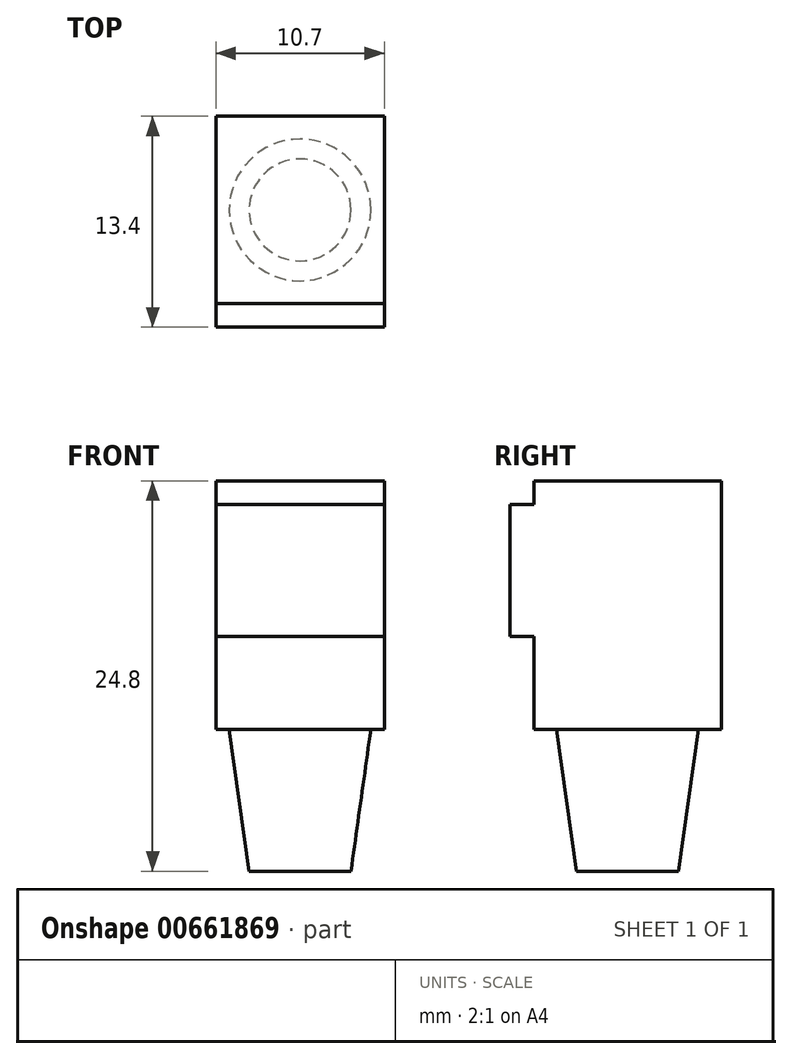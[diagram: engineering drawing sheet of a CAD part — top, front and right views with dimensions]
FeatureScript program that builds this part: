
annotation { "Feature Type Name" : "Feature", "Feature Type Description" : "" }
export const myFeature = defineFeature(function(context is Context, id is Id, definition is map)
    precondition{}
    {
        {
            var Q0;
            Q0=qCreatedBy(makeId("Right.planeOp"),FACE);
            var sketch = newSketch(context, id + "F0", { "sketchPlane" : qUnion([Q0])});
            skLineSegment(sketch, "E0", {"start": v(0, 0) * mm, "end": v(-16.33, 0) * mm, "construction": true});
            skLineSegment(sketch, "E1.bottom", {"start": v(1.5, 5.7) * mm, "end": v(13.4, 5.7) * mm});
            skLineSegment(sketch, "E1.top", {"start": v(1.5, -10.1) * mm, "end": v(13.4, -10.1) * mm});
            skLineSegment(sketch, "E1.left", {"start": v(1.5, 5.7) * mm, "end": v(1.5, 4.2) * mm});
            skLineSegment(sketch, "E1.right", {"start": v(13.4, 5.7) * mm, "end": v(13.4, -10.1) * mm});
            skLineSegment(sketch, "E2.bottom", {"start": v(0, 4.2) * mm, "end": v(1.5, 4.2) * mm});
            skLineSegment(sketch, "E2.top", {"start": v(0, -4.2) * mm, "end": v(1.5, -4.2) * mm});
            skLineSegment(sketch, "E2.left", {"start": v(0, 4.2) * mm, "end": v(0, -4.2) * mm});
            skLineSegment(sketch, "E3.trimOffspring", {"start": v(1.5, -4.2) * mm, "end": v(1.5, -10.1) * mm});
            skSolve(sketch);
        }
        {
            var Q0;
            Q0 = qSketchRegion(id + "F0", true);
            extrude(context, id + "F1", {"entities" : qUnion([Q0]), "depth" : 10.7 * mm, "offsetDistance" : 25 * mm, "symmetric" : true});
        }
        {
            var Q0;
            Q0=qCreatedBy(makeId("Right.planeOp"),FACE);
            var sketch = newSketch(context, id + "F2", { "sketchPlane" : qUnion([Q0])});
            skLineSegment(sketch, "E4", {"start": v(7.45, 9.05) * mm, "end": v(7.45, -10.1) * mm, "construction": true});
            skLineSegment(sketch, "E5", {"start": v(7.45, -10.1) * mm, "end": v(7.45, -19.1) * mm});
            skLineSegment(sketch, "E6", {"start": v(7.45, -19.1) * mm, "end": v(10.69, -19.1) * mm});
            skLineSegment(sketch, "E7", {"start": v(10.69, -19.1) * mm, "end": v(11.95, -10.1) * mm});
            skLineSegment(sketch, "E8", {"start": v(11.95, -10.1) * mm, "end": v(7.45, -10.1) * mm});
            skSolve(sketch);
        }
        {
            var Q0;
            Q0 = qSketchRegion(id + "F2", true);
            var Q1;
            Q1=sQuery(id+"F2.wireOp",EDGE,"E4");
            revolve(context, id + "F3", {"operationType" : NewBodyOperationType.ADD, "surfaceOperationType" : NewSurfaceOperationType.NEW, "entities" : qUnion([Q0]), "axis" : qUnion([Q1]), "revolveType" : RevolveType.FULL});
        }
    });
